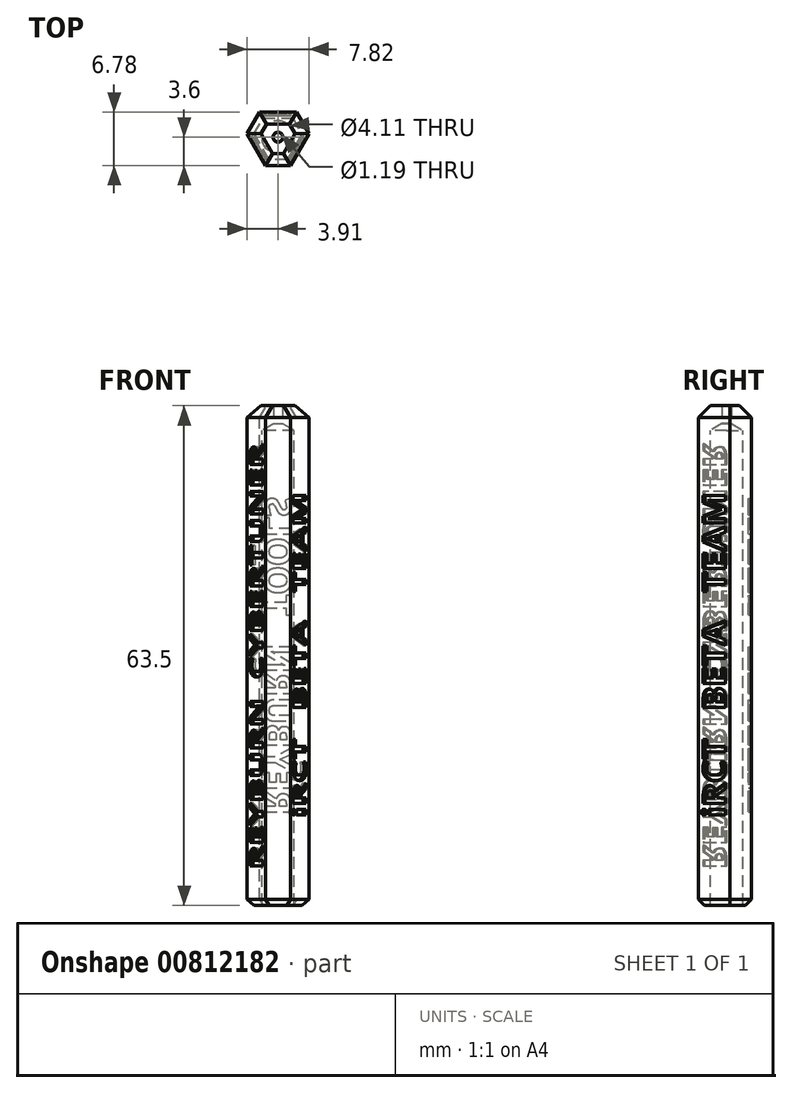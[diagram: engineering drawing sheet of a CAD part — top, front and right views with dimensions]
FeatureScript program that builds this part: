
annotation { "Feature Type Name" : "Feature", "Feature Type Description" : "" }
export const myFeature = defineFeature(function(context is Context, id is Id, definition is map)
    precondition{}
    {
        {
            var Q0;
            Q0=qCreatedBy(makeId("Top.planeOp"),FACE);
            var sketch = newSketch(context, id + "F0", { "sketchPlane" : qUnion([Q0])});
            skCircle(sketch, "E0.cCircle", {"center": v(0, 0) * mm, "radius": 6.35 * mm, "construction": true});
            skLineSegment(sketch, "E0.0", {"start": v(0, -6.35) * mm, "end": v(-5.5, 3.17) * mm});
            skLineSegment(sketch, "E0.1", {"start": v(-5.5, 3.18) * mm, "end": v(5.5, 3.18) * mm});
            skLineSegment(sketch, "E0.2", {"start": v(5.5, 3.18) * mm, "end": v(0, -6.35) * mm});
            skSolve(sketch);
        }
        {
            var Q0;
            Q0=makeQuery(id+"F0.imprint","IMPRINT",FACE,{"disambiguationData":[TD([[makeQuery(id+"F0.imprint","IMPRINT",EDGE,{"derivedFrom":sQuery(id+"F0.wireOp",EDGE,"E0.0")}),-1.0]])]});
            extrude(context, id + "F1", {"entities" : qUnion([Q0]), "oppositeDirection" : true, "depth" : 63.5 * mm, "offsetDistance" : 25.4 * mm});
        }
        {
            var Q0;
            Q0=makeQuery(id+"F1.opExtrude","CAP_FACE",FACE,{"disambiguationData":[OSD([sQuery(id+"F0.wireOp",EDGE,"E0.0"),sQuery(id+"F0.wireOp",EDGE,"E0.1"),sQuery(id+"F0.wireOp",EDGE,"E0.2")])],"isStart":false});
            var sketch = newSketch(context, id + "F2", { "sketchPlane" : qUnion([Q0])});
            skPoint(sketch, "E1", {"position": v(0, 0) * mm});
            skSolve(sketch);
        }
        {
            var Q0;
            Q0=sQuery(id+"F2.wireOp",VERTEX,"E1");
            var Q1;
            Q1=makeQuery(id+"F1.opExtrude","SWEPT_BODY",BODY,{"disambiguationData":[OSD([sQuery(id+"F0.wireOp",EDGE,"ghmTZ7Fa-hntI-yseL-cm0A-BedO1wdsdYtG")])]});
            var Q2;
            Q2=makeQuery(id+"F1.opExtrude","SWEPT_BODY",BODY,{"disambiguationData":[OSD([sQuery(id+"F0.wireOp",EDGE,"E0.0"),sQuery(id+"F0.wireOp",EDGE,"E0.1"),sQuery(id+"F0.wireOp",EDGE,"E0.2")])]});
            hole(context, id + "F3", {"style" : HoleStyle.C_SINK, "endStyle" : HoleEndStyle.BLIND, "holeDiameter" : 4.11 * mm, "cSinkDiameter" : 4.2 * mm, "cSinkAngle" : 90 * degree, "majorDiameter" : 6.35 * mm, "holeDepth" : 60.32 * mm, "isTappedThrough" : true, "tappedDepth" : 12.7 * mm, "tapClearance" : 3, "locations" : qUnion([Q0]), "scope" : qUnion([Q1, Q2]), "startStyle" : HoleStartStyle.PART});
        }
        {
            var Q0;
            Q0=makeQuery(id+"F1.opExtrude","SWEPT_EDGE",EDGE,{"disambiguationData":[OSD([sQuery(id+"F0.wireOp",EDGE,"E0.0"),sQuery(id+"F0.wireOp",EDGE,"E0.2")])]});
            var Q1;
            Q1=makeQuery(id+"F1.opExtrude","SWEPT_EDGE",EDGE,{"disambiguationData":[OSD([sQuery(id+"F0.wireOp",EDGE,"E0.1"),sQuery(id+"F0.wireOp",EDGE,"E0.2")])]});
            var Q2;
            Q2=makeQuery(id+"F1.opExtrude","SWEPT_EDGE",EDGE,{"disambiguationData":[OSD([sQuery(id+"F0.wireOp",EDGE,"E0.0"),sQuery(id+"F0.wireOp",EDGE,"E0.1")])]});
            chamfer(context, id + "F4", {"entities" : qUnion([Q0, Q1, Q2]), "width" : 3.17 * mm, "tangentPropagation" : true});
        }
        {
            var Q0;
            Q0=makeQuery(id+"F1.opExtrude","SWEPT_FACE",FACE,{"disambiguationData":[OSD([sQuery(id+"F0.wireOp",EDGE,"E0.1")])]});
            var sketch = newSketch(context, id + "F5", { "sketchPlane" : qUnion([Q0])});
            skText(sketch, "E2", { "text": "REYBURN   TOOLS", "fontName": "OpenSans-Bold.ttf"});
            skLineSegment(sketch, "E3", {"start": v(0, 0) * mm, "end": v(0, -11.5) * mm, "construction": true});
            skLineSegment(sketch, "E4", {"start": v(0, -63.5) * mm, "end": v(0, -52) * mm, "construction": true});
            const initialGuessF5  = {"E2": [0.00165, -0.052, 0, 1, 0.0033]};
            skSetInitialGuess(sketch, initialGuessF5);
            skSolve(sketch);
        }
        {
            var Q0;
            Q0=qSketchRegion(id+"F5",true);
            var Q1;
            Q1=qSketchRegion(id+"F7",true);
            extrude(context, id + "F6", {"entities" : qUnion([Q0, Q1]), "operationType" : NewBodyOperationType.REMOVE, "oppositeDirection" : true, "depth" : 0.43 * mm, "offsetDistance" : 25.4 * mm});
        }
        {
            var Q0;
            Q0=makeQuery(id+"F1.opExtrude","SWEPT_FACE",FACE,{"disambiguationData":[OSD([sQuery(id+"F0.wireOp",EDGE,"E0.0")])]});
            var sketch = newSketch(context, id + "F7", { "sketchPlane" : qUnion([Q0])});
            skText(sketch, "E5", { "text": "REYBURN  CYBERTUNER", "fontName": "OpenSans-Bold.ttf"});
            skLineSegment(sketch, "E6", {"start": v(0, 0) * mm, "end": v(0, -4.6) * mm, "construction": true});
            skLineSegment(sketch, "E7", {"start": v(0, -63.5) * mm, "end": v(0, -58.9) * mm});
            const initialGuessF7  = {"E5": [0.00165, -0.0589, 0, 1, 0.0033]};
            skSetInitialGuess(sketch, initialGuessF7);
            skSolve(sketch);
        }
        {
            var Q0;
            Q0=qSketchRegion(id+"F7",true);
            extrude(context, id + "F8", {"entities" : qUnion([Q0]), "operationType" : NewBodyOperationType.REMOVE, "oppositeDirection" : true, "depth" : 0.43 * mm, "offsetDistance" : 25.4 * mm});
        }
        {
            var Q0;
            Q0=makeQuery(id+"F1.opExtrude","SWEPT_FACE",FACE,{"disambiguationData":[OSD([sQuery(id+"F0.wireOp",EDGE,"E0.2")])]});
            var sketch = newSketch(context, id + "F9", { "sketchPlane" : qUnion([Q0])});
            skText(sketch, "E8", { "text": "iRCT   BETA   TEAM", "fontName": "OpenSans-Bold.ttf"});
            skLineSegment(sketch, "E9", {"start": v(0, -63.5) * mm, "end": v(0, -52.34) * mm, "construction": true});
            skLineSegment(sketch, "E10", {"start": v(0, 0) * mm, "end": v(0, -11.16) * mm, "construction": true});
            const initialGuessF9  = {"E8": [0.00165, -0.05234, 0, 1, 0.0033]};
            skSetInitialGuess(sketch, initialGuessF9);
            skSolve(sketch);
        }
        {
            var Q0;
            Q0=qSketchRegion(id+"F9",true);
            extrude(context, id + "F10", {"entities" : qUnion([Q0]), "operationType" : NewBodyOperationType.REMOVE, "oppositeDirection" : true, "depth" : 0.43 * mm, "offsetDistance" : 25.4 * mm});
        }
        {
            var Q0;
            Q0=makeQuery(id+"F1.opExtrude","CAP_FACE",FACE,{"disambiguationData":[OSD([sQuery(id+"F0.wireOp",EDGE,"E0.0"),sQuery(id+"F0.wireOp",EDGE,"E0.1"),sQuery(id+"F0.wireOp",EDGE,"E0.2")])],"isStart":true});
            var sketch = newSketch(context, id + "F11", { "sketchPlane" : qUnion([Q0])});
            skPoint(sketch, "E11", {"position": v(0, 0) * mm});
            skSolve(sketch);
        }
        {
            var Q0;
            Q0=sQuery(id+"F11.wireOp",VERTEX,"E11");
            var Q1;
            Q1=makeQuery(id+"F1.opExtrude","SWEPT_BODY",BODY,{"disambiguationData":[OSD([sQuery(id+"F0.wireOp",EDGE,"E0.0"),sQuery(id+"F0.wireOp",EDGE,"E0.1"),sQuery(id+"F0.wireOp",EDGE,"E0.2")])]});
            hole(context, id + "F12", {"style" : HoleStyle.C_SINK, "endStyle" : HoleEndStyle.THROUGH, "holeDiameter" : 1.2 * mm, "cSinkDiameter" : 1.27 * mm, "cSinkAngle" : 90 * degree, "majorDiameter" : 6.35 * mm, "isTappedThrough" : true, "tappedDepth" : 12.7 * mm, "tapClearance" : 3, "locations" : qUnion([Q0]), "scope" : qUnion([Q1]), "startStyle" : HoleStartStyle.PART});
        }
        {
            var Q0;
            Q0=makeQuery(id+"F1.opExtrude","CAP_EDGE",EDGE,{"disambiguationData":[OSD([sQuery(id+"F0.wireOp",EDGE,"E0.0")])],"isStart":false});
            var Q1;
            {var subQ0=sQuery(id+"F0.wireOp",EDGE,"E0.1");var subQ1=sQuery(id+"F0.wireOp",EDGE,"E0.0");Q1=makeQuery(id+"F4.opChamfer","BLEND_EDGE",EDGE,{"blendedFrom":[makeQuery(id+"F1.opExtrude","SWEPT_EDGE",EDGE,{"disambiguationData":[OSD([subQ1,subQ0])]}),makeQuery(id+"F1.opExtrude","CAP_FACE",FACE,{"disambiguationData":[OSD([subQ1,subQ0,sQuery(id+"F0.wireOp",EDGE,"E0.2")])],"isStart":false})],"blendedInto":[makeQuery(id+"F1.opExtrude","CAP_FACE",FACE,{"disambiguationData":[OSD([subQ1,subQ0,sQuery(id+"F0.wireOp",EDGE,"E0.2")])],"isStart":false})]});}
            var Q2;
            Q2=makeQuery(id+"F1.opExtrude","CAP_EDGE",EDGE,{"disambiguationData":[OSD([sQuery(id+"F0.wireOp",EDGE,"E0.1")])],"isStart":false});
            var Q3;
            {var subQ0=sQuery(id+"F0.wireOp",EDGE,"E0.2");var subQ1=sQuery(id+"F0.wireOp",EDGE,"E0.1");Q3=makeQuery(id+"F4.opChamfer","BLEND_EDGE",EDGE,{"blendedFrom":[makeQuery(id+"F1.opExtrude","SWEPT_EDGE",EDGE,{"disambiguationData":[OSD([subQ1,subQ0])]}),makeQuery(id+"F1.opExtrude","CAP_FACE",FACE,{"disambiguationData":[OSD([sQuery(id+"F0.wireOp",EDGE,"E0.0"),subQ1,subQ0])],"isStart":false})],"blendedInto":[makeQuery(id+"F1.opExtrude","CAP_FACE",FACE,{"disambiguationData":[OSD([sQuery(id+"F0.wireOp",EDGE,"E0.0"),subQ1,subQ0])],"isStart":false})]});}
            var Q4;
            Q4=makeQuery(id+"F1.opExtrude","CAP_EDGE",EDGE,{"disambiguationData":[OSD([sQuery(id+"F0.wireOp",EDGE,"E0.2")])],"isStart":false});
            var Q5;
            {var subQ0=sQuery(id+"F0.wireOp",EDGE,"E0.2");var subQ1=sQuery(id+"F0.wireOp",EDGE,"E0.0");Q5=makeQuery(id+"F4.opChamfer","BLEND_EDGE",EDGE,{"blendedFrom":[makeQuery(id+"F1.opExtrude","SWEPT_EDGE",EDGE,{"disambiguationData":[OSD([subQ1,subQ0])]}),makeQuery(id+"F1.opExtrude","CAP_FACE",FACE,{"disambiguationData":[OSD([subQ1,sQuery(id+"F0.wireOp",EDGE,"E0.1"),subQ0])],"isStart":false})],"blendedInto":[makeQuery(id+"F1.opExtrude","CAP_FACE",FACE,{"disambiguationData":[OSD([subQ1,sQuery(id+"F0.wireOp",EDGE,"E0.1"),subQ0])],"isStart":false})]});}
            chamfer(context, id + "F13", {"entities" : qUnion([Q0, Q1, Q2, Q3, Q4, Q5]), "width" : 0.76 * mm, "tangentPropagation" : true});
        }
        {
            var Q0;
            Q0=makeQuery(id+"F1.opExtrude","CAP_EDGE",EDGE,{"disambiguationData":[OSD([sQuery(id+"F0.wireOp",EDGE,"E0.2")])],"isStart":true});
            var Q1;
            {var subQ0=sQuery(id+"F0.wireOp",EDGE,"E0.2");var subQ1=sQuery(id+"F0.wireOp",EDGE,"E0.0");Q1=makeQuery(id+"F4.opChamfer","BLEND_EDGE",EDGE,{"blendedFrom":[makeQuery(id+"F1.opExtrude","SWEPT_EDGE",EDGE,{"disambiguationData":[OSD([subQ1,subQ0])]}),makeQuery(id+"F1.opExtrude","CAP_FACE",FACE,{"disambiguationData":[OSD([subQ1,sQuery(id+"F0.wireOp",EDGE,"E0.1"),subQ0])],"isStart":true})],"blendedInto":[makeQuery(id+"F1.opExtrude","CAP_FACE",FACE,{"disambiguationData":[OSD([subQ1,sQuery(id+"F0.wireOp",EDGE,"E0.1"),subQ0])],"isStart":true})]});}
            var Q2;
            Q2=makeQuery(id+"F1.opExtrude","CAP_EDGE",EDGE,{"disambiguationData":[OSD([sQuery(id+"F0.wireOp",EDGE,"E0.0")])],"isStart":true});
            var Q3;
            {var subQ0=sQuery(id+"F0.wireOp",EDGE,"E0.1");var subQ1=sQuery(id+"F0.wireOp",EDGE,"E0.0");Q3=makeQuery(id+"F4.opChamfer","BLEND_EDGE",EDGE,{"blendedFrom":[makeQuery(id+"F1.opExtrude","SWEPT_EDGE",EDGE,{"disambiguationData":[OSD([subQ1,subQ0])]}),makeQuery(id+"F1.opExtrude","CAP_FACE",FACE,{"disambiguationData":[OSD([subQ1,subQ0,sQuery(id+"F0.wireOp",EDGE,"E0.2")])],"isStart":true})],"blendedInto":[makeQuery(id+"F1.opExtrude","CAP_FACE",FACE,{"disambiguationData":[OSD([subQ1,subQ0,sQuery(id+"F0.wireOp",EDGE,"E0.2")])],"isStart":true})]});}
            var Q4;
            Q4=makeQuery(id+"F1.opExtrude","CAP_EDGE",EDGE,{"disambiguationData":[OSD([sQuery(id+"F0.wireOp",EDGE,"E0.1")])],"isStart":true});
            var Q5;
            {var subQ0=sQuery(id+"F0.wireOp",EDGE,"E0.2");var subQ1=sQuery(id+"F0.wireOp",EDGE,"E0.1");Q5=makeQuery(id+"F4.opChamfer","BLEND_EDGE",EDGE,{"blendedFrom":[makeQuery(id+"F1.opExtrude","SWEPT_EDGE",EDGE,{"disambiguationData":[OSD([subQ1,subQ0])]}),makeQuery(id+"F1.opExtrude","CAP_FACE",FACE,{"disambiguationData":[OSD([sQuery(id+"F0.wireOp",EDGE,"E0.0"),subQ1,subQ0])],"isStart":true})],"blendedInto":[makeQuery(id+"F1.opExtrude","CAP_FACE",FACE,{"disambiguationData":[OSD([sQuery(id+"F0.wireOp",EDGE,"E0.0"),subQ1,subQ0])],"isStart":true})]});}
            chamfer(context, id + "F14", {"entities" : qUnion([Q0, Q1, Q2, Q3, Q4, Q5]), "width" : 1.52 * mm, "tangentPropagation" : true});
        }
    });
